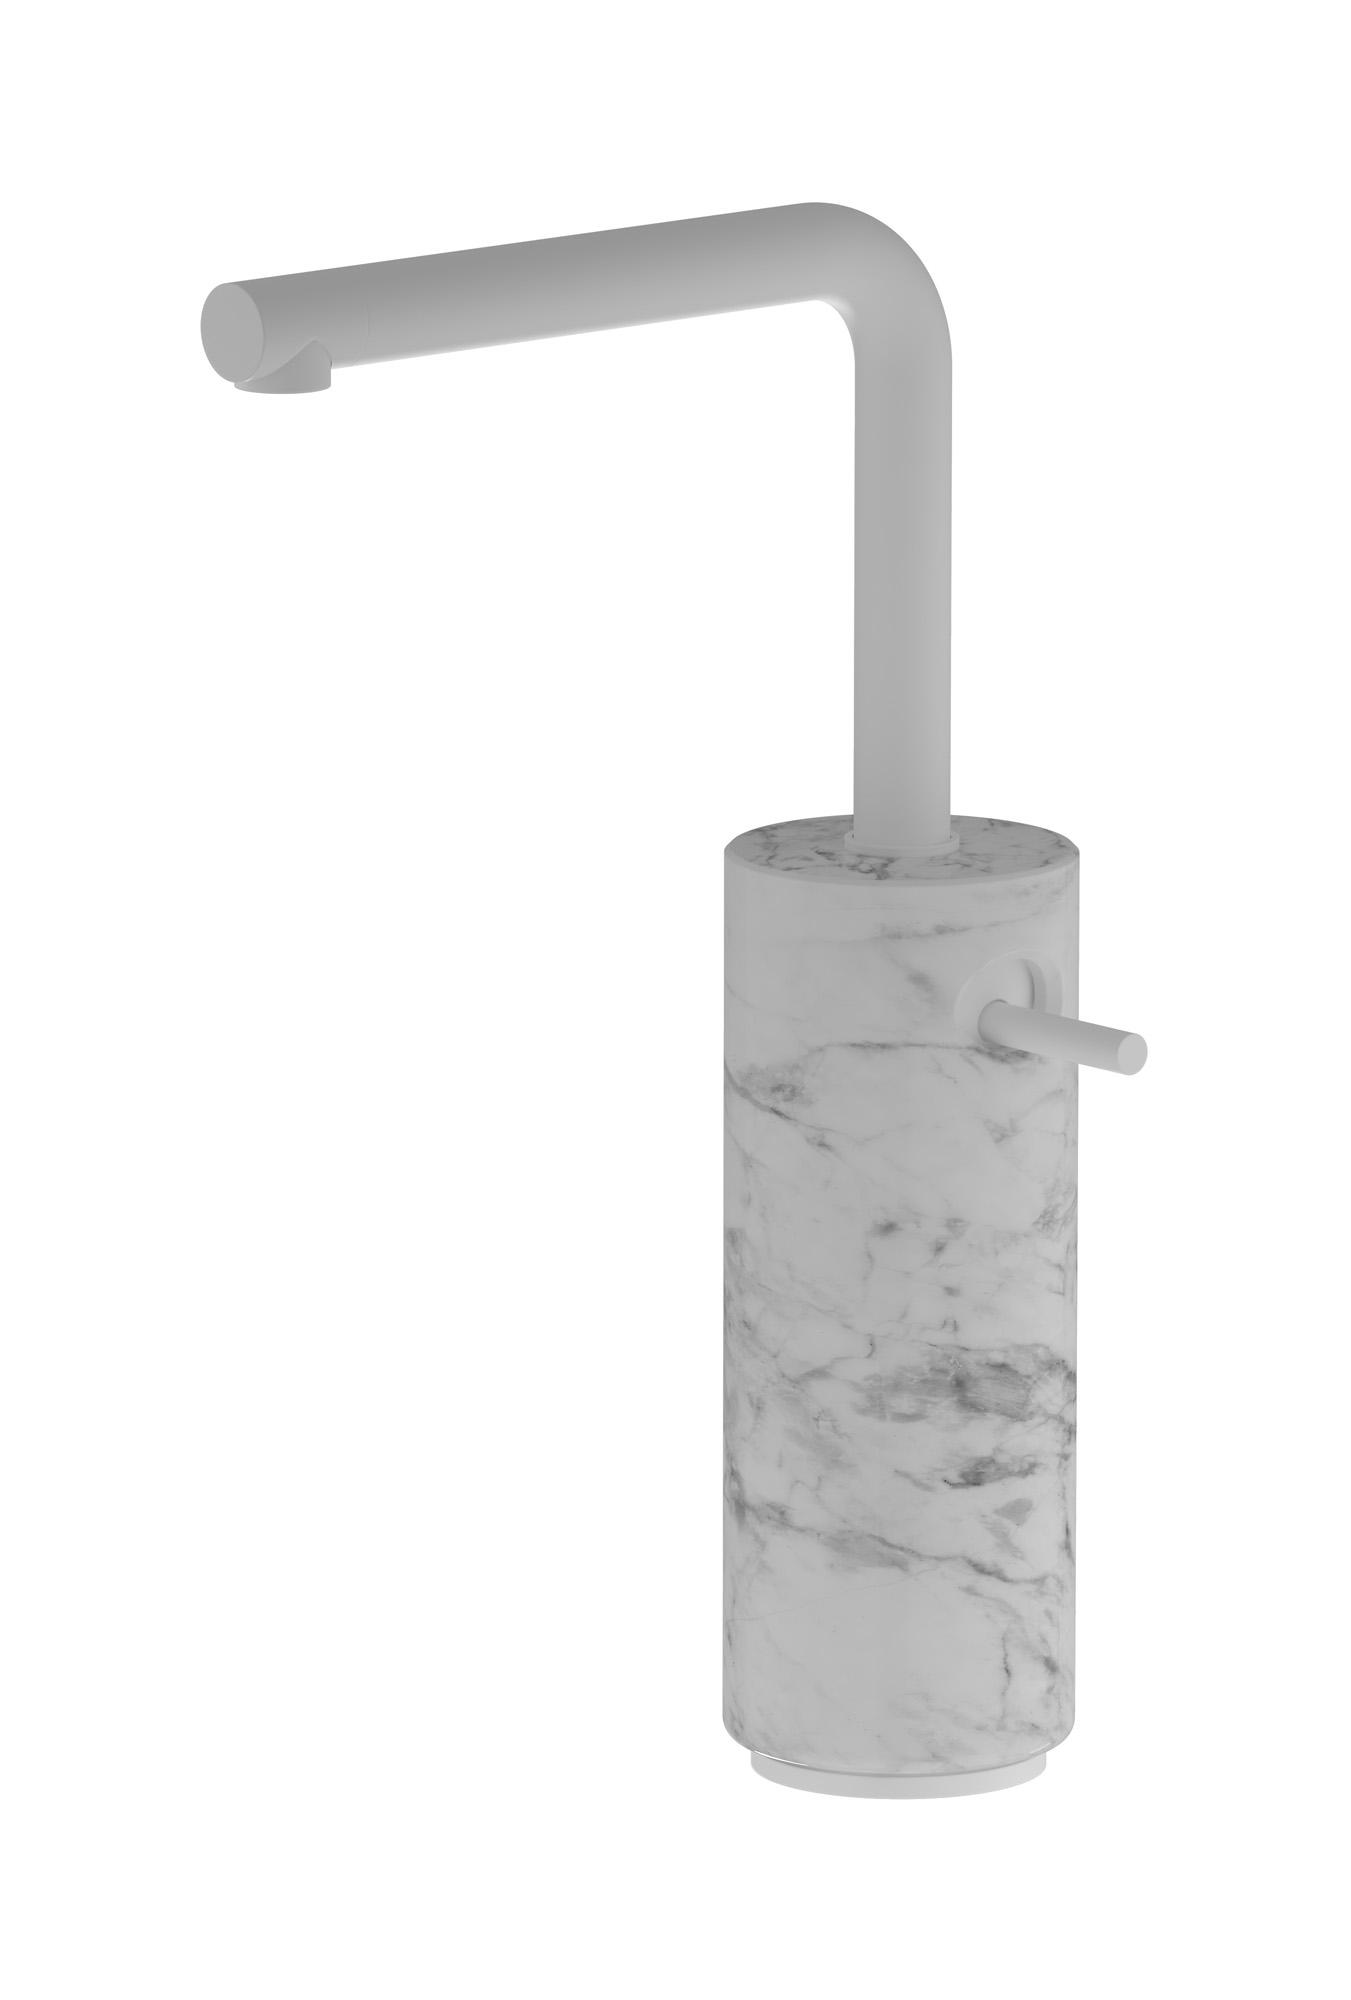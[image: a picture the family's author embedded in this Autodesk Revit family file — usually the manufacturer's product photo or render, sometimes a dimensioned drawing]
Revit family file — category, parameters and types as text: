
# Revit family: MM202_1
name_source: partatom
category: Apparecchi idraulici
units: mm (PartAtom-declared; Revit-internal decimal feet)

## family parameters
Basato su piano di lavoro = No
Condiviso = No
Mantieni orientamento annotazione = No
Numero OmniClass = 23.45.55.17
Punto di calcolo locali = No
Quota connettore circolare = Usa diametro
Sempre verticale = Sì
Taglio con vuoti quando caricato = No
Tipo di parte = Normale
Titolo OmniClass = Mixing Faucets

## types (14) — shared parameters
Cold water inlet = 10 mm  [stored 0.0328084 ft]
Commenti sul tipo = Washbasin mixer
Connessione CW = No
Connessione HW = No
Connessione di scarico = No
Connessione di ventilazione = No
Descrizione = Tall monohole washbasin mixer
Hot water inlet = 10 mm  [stored 0.0328084 ft]
Produttore = IB Rubinetterie S.p.A.
URL = https://www.weareib.it
zero-valued in all types: Prospetto di default

## per-type parameters (varying)
| type | Finishes surface | Immagine tipo | Modello |
| Chrome | IB_Chrome | MM202CC_1.jpg | MM202CC_1 |
| Platinum | IB_Platinum | MM202PL_1.jpg | MM202PL_1 |
| Brushed nickel | IB_Brushed nickel | MM202SS_1.jpg | MM202SS_1 |
| Natural brass | IB_Brass | MM202ON_1.jpg | MM202ON_1 |
| Matt white | IB_matt white | MM202BO_1.jpg | MM202BO_1 |
| Matt black | IB_matt black | MM202NP_1.jpg | MM202NP_1 |
| Black chrome | IB_Black chrome | MM202CF_1.jpg | MM202CF_1 |
| Brushed black chrome | IB_Brushed black chrome | MM202CS_1.jpg | MM202CS_1 |
| Pale gold | IB_Pale gold | MM202II_1.jpg | MM202II_1 |
| Brushed pale gold | IB_brushed pale gold | MM202IS_1.jpg | MM202IS_1 |
| Rose gold | IB_Rose gold | MM202RS_1.jpg | MM202RS_1 |
| Brushed rose gold | IB_Brushed rose gold | MM202SR_1.jpg | MM202SR_1 |
| Gold | IB_gold | MM202OO_1.jpg | MM202OO_1 |
| Brushed gold | IB_brushed gold | MM202OS_1.jpg | MM202OS_1 |

note: [stored X ft] marks values corroborated as IEEE doubles in the binary element streams (Revit-internal decimal feet)
